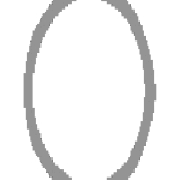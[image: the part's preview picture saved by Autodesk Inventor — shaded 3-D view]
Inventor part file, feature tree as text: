
AUTODESK INVENTOR PART (.ipt)
format: ipt  version: 2021 (Build 250183000, 183)  size: 109,568 bytes
history: native  units: in
note: dims shown in document units (in); Inventor stores cm internally (conversion verified against a paired STEP export)
features: other x4, sketch x3, plane x1
ambient origin geometry x8: Origin, YZ Plane, XZ Plane, XY Plane, X Axis, Y Axis, Z Axis, Center Point
bodies: Solid1 (feature_tree), Body (feature_tree)
feature tree (8):
  other  "Driven Length"
  other  "Frame Generator"
  other  "Start Plane"
  other  "End Plane"
  sketch  "Sketch"  dims[d2=20.0811in d4=-0.0in d5=20.0811in d6=0.12in d7=0.0in d8=90.0deg d9=20.0811in]
  sketch  "Sketch2"  dims[d0=1.0in]
  plane  "Work Plane3"
  sketch  "Sketch3"  dims[d1=0.065in]
